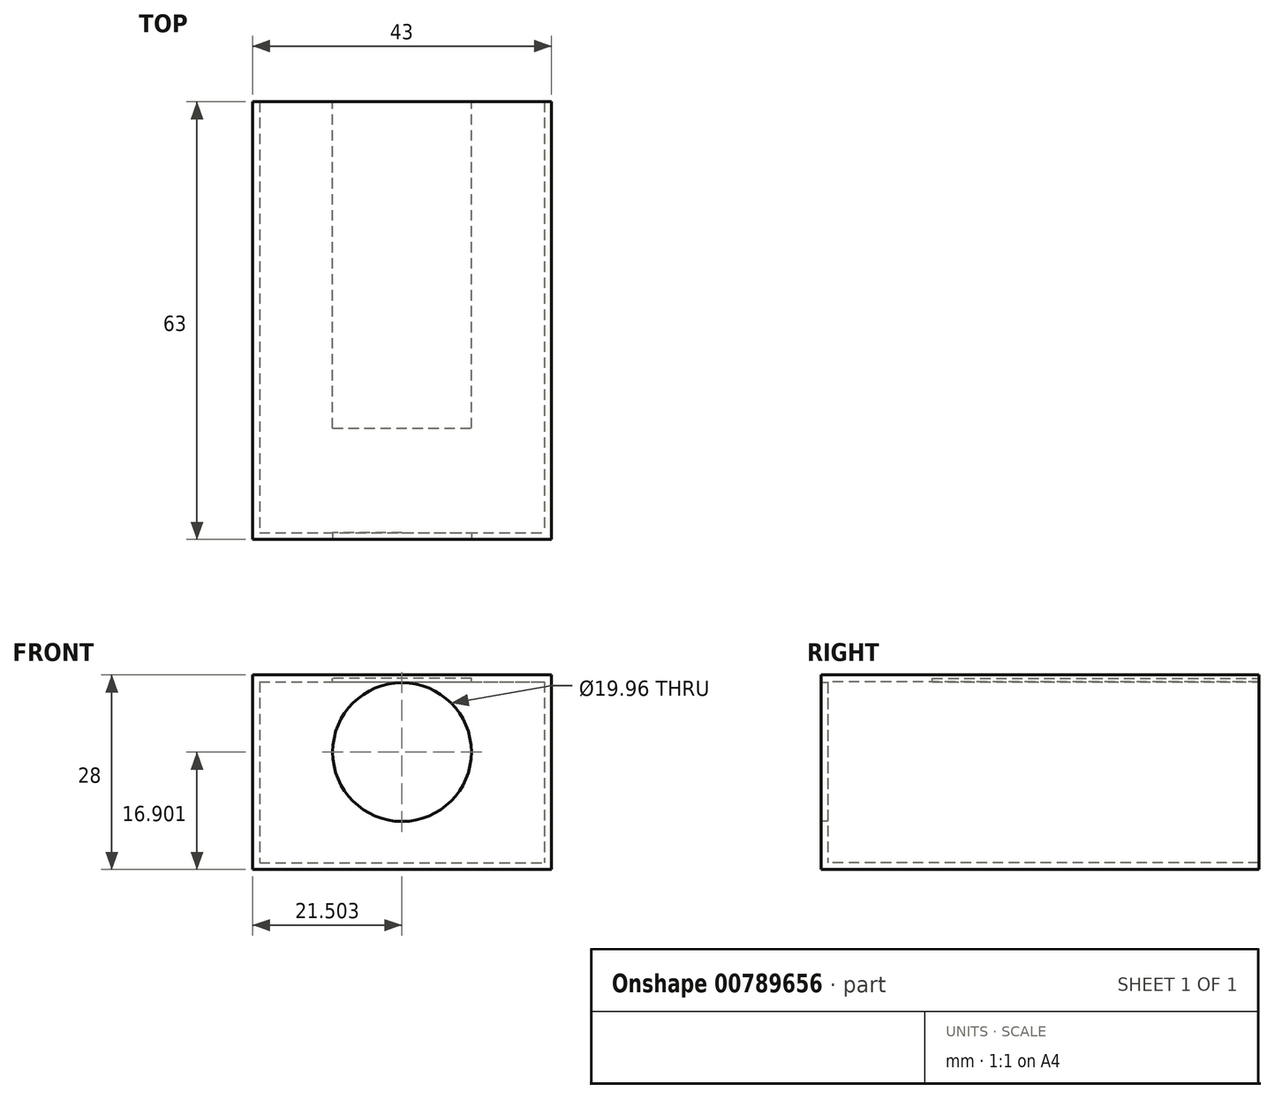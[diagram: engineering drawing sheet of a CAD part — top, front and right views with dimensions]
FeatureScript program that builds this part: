
annotation { "Feature Type Name" : "Feature", "Feature Type Description" : "" }
export const myFeature = defineFeature(function(context is Context, id is Id, definition is map)
    precondition{}
    {
        {
            var Q0;
            Q0=qCreatedBy(makeId("Top.planeOp"),FACE);
            var sketch = newSketch(context, id + "F0", { "sketchPlane" : qUnion([Q0])});
            skLineSegment(sketch, "E0.bottom", {"start": v(4.96, 25.33) * mm, "end": v(47.96, 25.33) * mm});
            skLineSegment(sketch, "E0.top", {"start": v(4.96, -37.67) * mm, "end": v(47.96, -37.67) * mm});
            skLineSegment(sketch, "E0.left", {"start": v(4.96, 25.33) * mm, "end": v(4.96, -37.67) * mm});
            skLineSegment(sketch, "E0.right", {"start": v(47.96, 25.33) * mm, "end": v(47.96, -37.67) * mm});
            skSolve(sketch);
        }
        {
            var Q0;
            Q0=makeQuery(id+"F0.imprint","IMPRINT",FACE,{"disambiguationData":[TD([[makeQuery(id+"F0.imprint","IMPRINT",EDGE,{"derivedFrom":sQuery(id+"F0.wireOp",EDGE,"E0.bottom")}),-1.0]])]});
            extrude(context, id + "F1", {"entities" : qUnion([Q0]), "depth" : 28 * mm, "offsetDistance" : 25 * mm});
        }
        {
            var Q0;
            Q0=makeQuery(id+"F1.opExtrude","SWEPT_FACE",FACE,{"disambiguationData":[OSD([sQuery(id+"F0.wireOp",EDGE,"E0.top")])]});
            var sketch = newSketch(context, id + "F2", { "sketchPlane" : qUnion([Q0])});
            skLineSegment(sketch, "E1", {"start": v(4.96, 28) * mm, "end": v(26.46, 28) * mm});
            skCircle(sketch, "E2", {"center": v(26.46, 16.9) * mm, "radius": 9.98 * mm});
            skSolve(sketch);
        }
        {
            var Q0;
            Q0=makeQuery(id+"F2.imprint","IMPRINT",FACE,{"disambiguationData":[TD([[makeQuery(id+"F2.imprint","IMPRINT",EDGE,{"derivedFrom":sQuery(id+"F2.wireOp",EDGE,"E2")}),1.0]])]});
            extrude(context, id + "F3", {"entities" : qUnion([Q0]), "operationType" : NewBodyOperationType.REMOVE, "oppositeDirection" : true, "depth" : 63 * mm, "offsetDistance" : 25 * mm});
        }
        {
            var Q0;
            Q0=makeQuery(id+"F3.boolean.opBoolean","COPY",FACE,{"derivedFrom":makeQuery(id+"F3.opExtrude","SWEPT_FACE",FACE,{"disambiguationData":[OSD([sQuery(id+"F2.wireOp",EDGE,"E2")])]})});
            var Q1;
            Q1=makeQuery(id+"F1.opExtrude","SWEPT_FACE",FACE,{"disambiguationData":[OSD([sQuery(id+"F0.wireOp",EDGE,"E0.bottom")])]});
            shell(context, id + "F4", {"entities" : qUnion([Q0, Q1]), "thickness" : 1 * mm});
        }
        {
            var Q0;
            Q0=makeQuery(id+"F1.opExtrude","SWEPT_FACE",FACE,{"disambiguationData":[OSD([sQuery(id+"F0.wireOp",EDGE,"E0.bottom")])]});
            var sketch = newSketch(context, id + "F5", { "sketchPlane" : qUnion([Q0])});
            skLineSegment(sketch, "E3", {"start": v(-26.46, 27) * mm, "end": v(-36.46, 27) * mm});
            skLineSegment(sketch, "E4.bottom", {"start": v(-36.46, 27) * mm, "end": v(-16.46, 27) * mm});
            skLineSegment(sketch, "E4.top", {"start": v(-36.46, 27.5) * mm, "end": v(-16.46, 27.5) * mm});
            skLineSegment(sketch, "E4.left", {"start": v(-36.46, 27) * mm, "end": v(-36.46, 27.5) * mm});
            skLineSegment(sketch, "E4.right", {"start": v(-16.46, 27) * mm, "end": v(-16.46, 27.5) * mm});
            skSolve(sketch);
        }
        {
            var Q0;
            Q0=makeQuery(id+"F5.imprint","IMPRINT",FACE,{"disambiguationData":[TD([[makeQuery(id+"F5.imprint","IMPRINT",EDGE,{"derivedFrom":sQuery(id+"F5.wireOp",EDGE,"E4.top")}),-1.0]])]});
            extrude(context, id + "F6", {"entities" : qUnion([Q0]), "operationType" : NewBodyOperationType.REMOVE, "oppositeDirection" : true, "depth" : 47 * mm, "offsetDistance" : 25 * mm});
        }
    });
